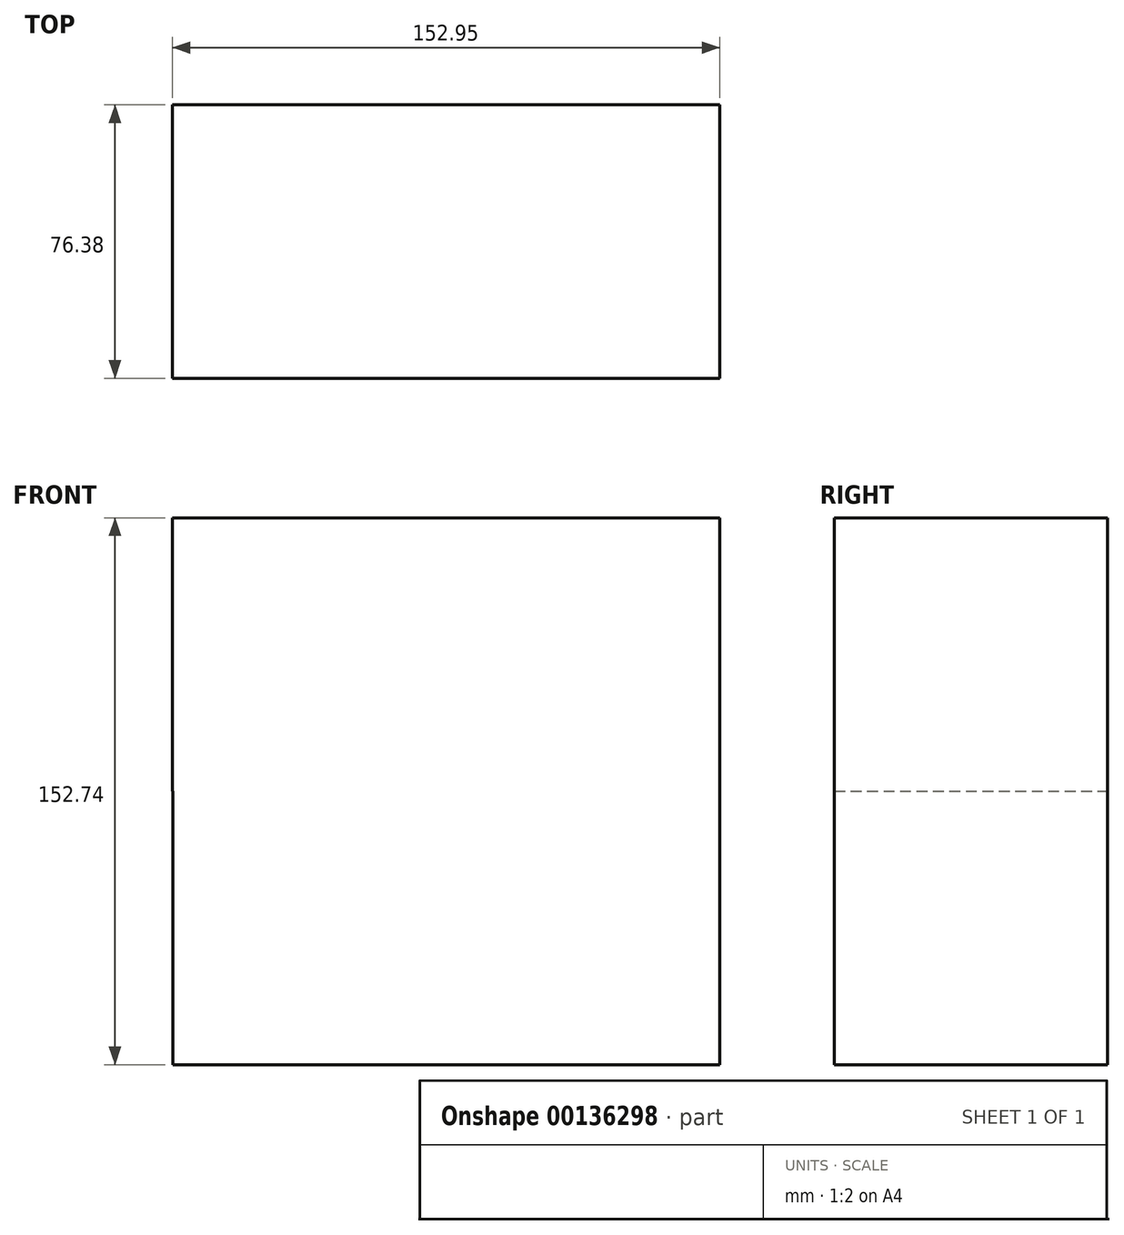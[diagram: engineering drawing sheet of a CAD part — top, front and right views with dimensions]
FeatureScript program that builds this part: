
annotation { "Feature Type Name" : "Feature", "Feature Type Description" : "" }
export const myFeature = defineFeature(function(context is Context, id is Id, definition is map)
    precondition{}
    {
        {
            var Q0;
            Q0=qCreatedBy(makeId("Front.planeOp"),FACE);
            var sketch = newSketch(context, id + "F0", { "sketchPlane" : qUnion([Q0])});
            skLineSegment(sketch, "E0.bottom", {"start": v(0, 0) * mm, "end": v(76.37, 0) * mm});
            skLineSegment(sketch, "E0.top", {"start": v(0, 76.37) * mm, "end": v(76.37, 76.37) * mm});
            skLineSegment(sketch, "E0.left", {"start": v(0, 0) * mm, "end": v(0, 76.37) * mm});
            skLineSegment(sketch, "E0.right", {"start": v(76.37, 0) * mm, "end": v(76.37, 76.37) * mm});
            skLineSegment(sketch, "E1.bottom", {"start": v(0, 0) * mm, "end": v(-76.58, 0) * mm});
            skLineSegment(sketch, "E1.top", {"start": v(0, 76.37) * mm, "end": v(-76.58, 76.37) * mm});
            skLineSegment(sketch, "E1.right", {"start": v(-76.58, 0) * mm, "end": v(-76.58, 76.37) * mm});
            skLineSegment(sketch, "E2.top", {"start": v(0, -76.37) * mm, "end": v(76.37, -76.37) * mm});
            skLineSegment(sketch, "E2.left", {"start": v(0, 0) * mm, "end": v(0, -76.37) * mm});
            skLineSegment(sketch, "E2.right", {"start": v(76.37, 0) * mm, "end": v(76.37, -76.37) * mm});
            skLineSegment(sketch, "E3.bottom", {"start": v(0, 0) * mm, "end": v(-76.37, 0) * mm});
            skLineSegment(sketch, "E3.top", {"start": v(0, -76.37) * mm, "end": v(-76.37, -76.37) * mm});
            skLineSegment(sketch, "E3.right", {"start": v(-76.37, 0) * mm, "end": v(-76.37, -76.37) * mm});
            skSolve(sketch);
        }
        {
            var Q0;
            Q0 = qSketchRegion(id + "F0", true);
            extrude(context, id + "F1", {"entities" : qUnion([Q0]), "depth" : 76.38 * mm});
        }
    });
